# Revit family: Fireplace_Insert
name_source: partatom
category: Generic Models
units: mm (PartAtom-declared; Revit-internal decimal feet)

## family parameters
Always vertical = Yes
Can host rebar = No
Cut with Voids When Loaded = No
Host = Wall
Maintain Annotation Orientation = No
Part Type = Normal
Room Calculation Point = No
Round Connector Dimension = Use Diameter
Shared = No

## types (1)
- Fireplace_Insert
    Construction Details = http://www.arcat.com
    Default Elevation = 0' - 0"
    Expected Lifespan (Years) = 0
    Firebox Height = 4' - 8 7/16"
    Firebox Width = 2' - 6"
    Green Building-LEED = http://www.arcat.com
    Gross Depth = 1' - 3"
    Gross Height = 4' - 8 7/16"
    Gross Projection = 1' - 3"
    Gross Width = 6' - 8 3/32"
    Maintenance Schedule (Months) = 0
    Mantle Thickness = 0' - 11"
    Manufacturer = Generic
    Manufacturer Fax = (203) 929-2444
    Manufacturer Website = http://www.arcat.com
    Model = Generic
    Product Data = http://www.arcat.com
    Product Properties = http://www.arcat.com
    Specification = http://www.arcat.com
    Warranty Duration (Years) = 0
    gratefins = 30

## geometry (parser evidence)
native form markers: Sweep x4
no freeform markers — native parametric forms only
